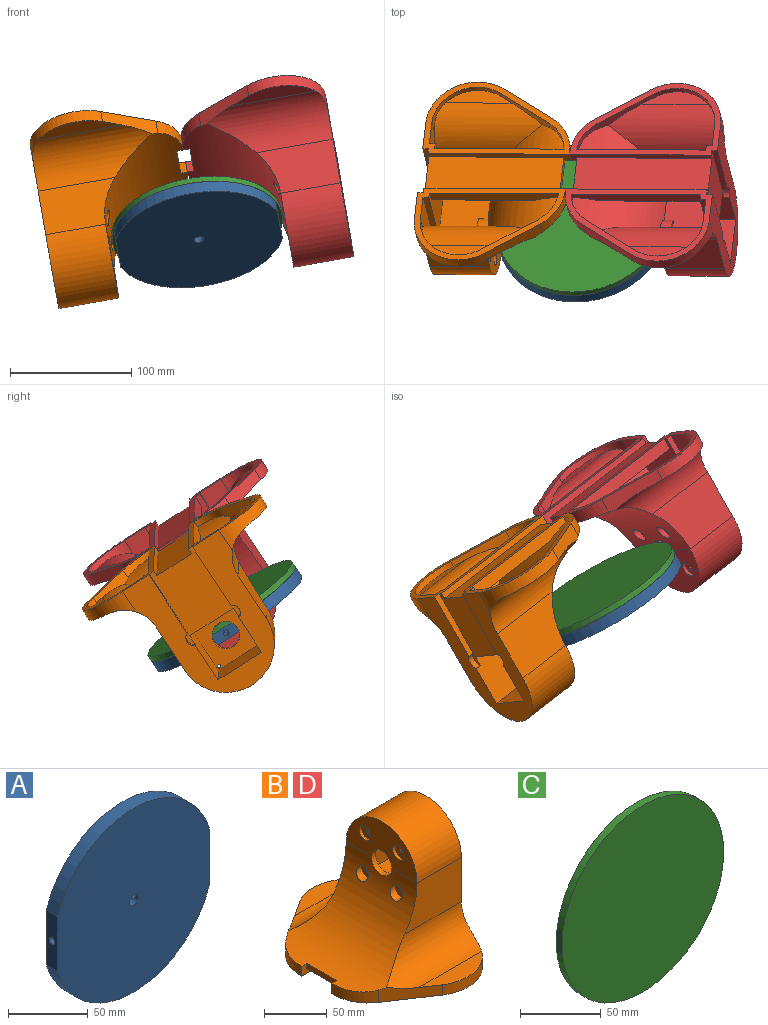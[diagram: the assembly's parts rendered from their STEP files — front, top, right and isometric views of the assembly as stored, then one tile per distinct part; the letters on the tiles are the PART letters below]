
ASSEMBLY  parts=4 mates=3
PART A: 14 faces, bbox 135x10.1x141.4 mm
  f0: cylinder r=2.5mm len=64.4mm, axis (-1,0,0), area 927.1mm2, adj f3,f9,f10,f11,f12,f13
  f1: cylinder r=2.5mm len=64.4mm, axis (-1,0,0), area 927.1mm2, adj f5,f9,f10,f11,f12,f13
  f2: plane 96.2x96.2mm, normal (0,1,0), area 7217.6mm2, adj f9,f11
  f3: plane 42x10mm, normal (1,0,0), area 400.4mm2, adj f0,f4,f6,f7,f8
  f4: cylinder r=70.71mm len=135.04mm, axis (0,1,0), area 1795mm2, adj f3,f5,f7,f8
  f5: plane 42x10mm, normal (-1,0,0), area 400.4mm2, adj f1,f4,f6,f7,f8
  f6: cylinder r=70.71mm len=135.04mm, axis (0,1,0), area 1795mm2, adj f3,f5,f7,f8
  f7: plane 141.42x135.04mm, normal (0,-1,0), area 15478.2mm2, adj f3,f4,f5,f6,f9
  f8: plane 141.42x135.04mm, normal (0,1,0), area 5641.8mm2, adj f3,f4,f5,f6,f12
  f9: cylinder r=4mm len=10mm, axis (0,1,0), area 209.8mm2, adj f0,f1,f2,f7
  f10: torus R=52.1mm, axis (0,-1,0), area 2003mm2, adj f0,f1,f11,f12
  f11: cylinder r=48.1mm len=96.2mm, axis (0,-1,0), area 816.8mm2, adj f0,f1,f2,f10,f13
  f12: cylinder r=56.1mm len=112.2mm, axis (0,-1,0), area 952.8mm2, adj f0,f1,f8,f10,f13
  f13: torus R=52.1mm, axis (0,-1,0), area 2003mm2, adj f0,f1,f11,f12
PART B: 93 faces, bbox 123.2x174.5x123.4 mm
  f0: plane 10x1.55mm, normal (-1,0,0), area 15.5mm2, adj f1,f2,f9,f36
  f1: cylinder r=73.21mm len=110.84mm, axis (0,1,0), area 9260.8mm2, adj f0,f7,f9,f11,f16,f17,f18,f21
  f2: plane 123.21x70.24mm, normal (0,0,-1), area 1573.2mm2, adj f0,f9,f10,f30,f35,f36,f43,f45
  f3: plane 123.21x70.24mm, normal (0,0,-1), area 1573.2mm2, adj f7,f10,f11,f32,f34,f38,f42,f45
  f4: plane 45.4x42.8mm, normal (0,-1,0), area 1901.8mm2, adj f6,f10,f19,f20,f44,f45
  f5: plane 45.4x42.8mm, normal (0,1,0), area 1901.8mm2, adj f6,f10,f19,f20,f41,f45
  f6: plane 42.8x40.5mm, normal (0,0,1), area 1733.4mm2, adj f4,f5,f20,f45
  f7: plane 118.31x10.21mm, normal (0,1,0), area 619.4mm2, adj f1,f3,f8,f11,f45,f84
  f8: plane 112.81x34mm, normal (0,0,-1), area 3835.6mm2, adj f7,f9,f45,f84
  f9: plane 118.31x10.21mm, normal (0,-1,0), area 619.4mm2, adj f0,f1,f2,f8,f45,f84
  f10: plane 123.36x94.48mm, normal (1,0,0), area 5011.8mm2, adj f2,f3,f4,f5,f17,f18,f19,f34
  f11: plane 10x1.55mm, normal (-1,0,0), area 15.5mm2, adj f1,f3,f7,f38
  f12: cylinder r=1.5mm len=3mm, axis (1,0,0), area 14.1mm2, adj f20,f25
  f13: cylinder r=1.5mm len=3mm, axis (1,0,0), area 14.1mm2, adj f20,f23
  f14: cylinder r=1.5mm len=3mm, axis (1,0,0), area 14.1mm2, adj f20,f29
  f15: cylinder r=1.5mm len=3mm, axis (1,0,0), area 14.1mm2, adj f20,f27
  f16: plane 80x40.15mm, normal (-1,0,0), area 2051.7mm2, adj f1,f17,f18,f21,f22,f24,f37
  f17: plane 64.11x43.36mm, normal (0,-1,0), area 2362.6mm2, adj f1,f10,f16,f37,f39
  f18: plane 64.11x43.36mm, normal (0,1,0), area 2362.6mm2, adj f1,f10,f16,f37,f40
  f19: plane 45.4x42.8mm, normal (0,0,-1), area 1943.1mm2, adj f4,f5,f10,f20
  f20: plane 42.8x42.8mm, normal (1,0,0), area 1388.1mm2, adj f4,f5,f6,f12,f13,f14,f15,f19
  f21: cylinder r=11.5mm len=23mm, axis (1,0,0), area 348.8mm2, adj f1,f16,f20
  f22: cylinder r=6.5mm len=13mm, axis (1,0,0), area 126.6mm2, adj f16,f23
  f23: plane 13x13mm, normal (-1,0,0), area 125.7mm2, adj f13,f22
  f24: cylinder r=6.5mm len=13mm, axis (1,0,0), area 126.6mm2, adj f16,f25
  f25: plane 13x13mm, normal (-1,0,0), area 125.7mm2, adj f12,f24
  f26: cylinder r=6.5mm len=13mm, axis (1,0,0), area 235.6mm2, adj f1,f27
  f27: plane 13x13mm, normal (-1,0,0), area 125.7mm2, adj f15,f26
  f28: cylinder r=6.5mm len=13mm, axis (1,0,0), area 235.6mm2, adj f1,f29
  f29: plane 13x13mm, normal (-1,0,0), area 125.7mm2, adj f14,f28
  f30: plane 43.23x28.71mm, normal (-0.55,0.83,0), area 570mm2, adj f1,f2,f31,f35,f36,f40
  f31: plane 70.92x17.24mm, normal (0,0,1), area 815.9mm2, adj f30,f35,f40
  f32: plane 43.23x28.71mm, normal (-0.55,-0.83,0), area 570mm2, adj f1,f3,f33,f34,f38,f39
  f33: plane 70.92x17.24mm, normal (0,0,1), area 815.9mm2, adj f32,f34,f39
  f34: cylinder r=40mm len=62.13mm, axis (0,0,-1), area 936.8mm2, adj f3,f10,f32,f33,f39
  f35: cylinder r=40mm len=62.13mm, axis (0,0,1), area 936.8mm2, adj f2,f10,f30,f31,f40
  f36: cylinder r=40mm len=33.32mm, axis (0,0,-1), area 412mm2, adj f0,f1,f2,f30
  f37: cylinder r=40mm len=80mm, axis (1,0,0), area 6283.2mm2, adj f10,f16,f17,f18
  f38: cylinder r=40mm len=33.32mm, axis (0,0,1), area 412mm2, adj f1,f3,f11,f32
  f39: cylinder r=30mm len=99.99mm, axis (-1,0,0), area 3860mm2, adj f1,f10,f17,f32,f33,f34
  f40: cylinder r=30mm len=99.99mm, axis (1,0,0), area 3860mm2, adj f1,f10,f18,f30,f31,f35
  f41: cylinder r=6.5mm len=12.06mm, axis (1,0,0), area 75.7mm2, adj f5,f10,f42,f45
  f42: plane 58.19x4.9mm, normal (0,1,0), area 285.1mm2, adj f3,f10,f41,f45
  f43: plane 58.19x4.9mm, normal (0,-1,0), area 285.1mm2, adj f2,f10,f44,f45
  f44: cylinder r=6.5mm len=12.06mm, axis (1,0,0), area 75.7mm2, adj f4,f10,f43,f45
  f45: plane 70.25x51mm, normal (1,0,0), area 2553.5mm2, adj f2,f3,f4,f5,f6,f7,f8,f9
  f46: plane 73.01x61mm, normal (-1,0,0), area 2665.9mm2, adj f2,f3,f47,f48,f49,f50,f70,f71
  f47: cylinder r=11.5mm len=17.56mm, axis (1,0,0), area 97.9mm2, adj f46,f48,f69,f81
  f48: plane 55.45x4.9mm, normal (0,1,0), area 271.7mm2, adj f2,f46,f47,f69
  f49: plane 55.45x4.9mm, normal (0,-1,0), area 271.7mm2, adj f3,f46,f50,f74
  f50: cylinder r=11.5mm len=17.56mm, axis (1,0,0), area 97.9mm2, adj f46,f49,f74,f78
  f51: cylinder r=35mm len=90.93mm, axis (1,0,0), area 3925mm2, adj f55,f59,f60,f66,f69,f82
  f52: cylinder r=35mm len=90.93mm, axis (-1,0,0), area 3925mm2, adj f56,f57,f58,f67,f74,f82
  f53: cylinder r=35mm len=25.7mm, axis (0,0,1), area 183.4mm2, adj f3,f58,f72,f82
  f54: cylinder r=35mm len=25.7mm, axis (0,0,-1), area 183.4mm2, adj f2,f60,f70,f82
  f55: cylinder r=35mm len=54.36mm, axis (0,0,1), area 439.2mm2, adj f2,f51,f59,f60,f69
  f56: cylinder r=35mm len=54.36mm, axis (0,0,-1), area 439.2mm2, adj f3,f52,f57,f58,f74
  f57: plane 55.58x12.24mm, normal (0,0,-1), area 457.2mm2, adj f52,f56,f58
  f58: plane 43.24x28.72mm, normal (0.55,0.83,0), area 340.9mm2, adj f3,f52,f53,f56,f57,f82
  f59: plane 55.58x12.24mm, normal (0,0,-1), area 457.2mm2, adj f51,f55,f60
  f60: plane 43.24x28.72mm, normal (0.55,-0.83,0), area 340.9mm2, adj f2,f51,f54,f55,f59,f82
  f61: cylinder r=11.5mm len=20.3mm, axis (1,0,0), area 272.4mm2, adj f73,f78,f82,f83
  f62: plane 20.3x20.3mm, normal (1,0,0), area 99.3mm2, adj f63,f73,f81
  f63: cylinder r=11.5mm len=20.3mm, axis (1,0,0), area 272.4mm2, adj f62,f73,f81,f82
  f64: plane 12.93x4mm, normal (1,0,0), area 31mm2, adj f65,f77,f78
  f65: cylinder r=11.5mm len=7.29mm, axis (1,0,0), area 26.4mm2, adj f64,f75,f77,f78
  f66: plane 53.02x43.36mm, normal (0,-1,0), area 1915.1mm2, adj f51,f68,f69,f76,f82
  f67: plane 53.02x43.36mm, normal (0,1,0), area 1915.1mm2, adj f52,f74,f75,f77,f82
  f68: plane 17.49x8.6mm, normal (1,0,0), area 105.6mm2, adj f66,f76,f79,f81,f82
  f69: plane 106.34x20.84mm, normal (-1,0,0), area 1062.8mm2, adj f2,f47,f48,f51,f55,f66,f76,f81
  f70: plane 108.14x10mm, normal (0,1,0), area 1014.6mm2, adj f2,f46,f54,f71,f82
  f71: plane 85.8x44mm, normal (0,0,1), area 3775mm2, adj f46,f70,f72,f82
  f72: plane 108.14x10mm, normal (0,-1,0), area 1014.6mm2, adj f3,f46,f53,f71,f82
  f73: plane 52.8x39.69mm, normal (0,0,-1), area 1846.4mm2, adj f46,f61,f62,f63,f78,f81,f82,f83
  f74: plane 106.34x20.84mm, normal (-1,0,0), area 1062.8mm2, adj f3,f49,f50,f52,f56,f67,f77,f78
  f75: plane 17.49x8.6mm, normal (1,0,0), area 105.6mm2, adj f65,f67,f77,f78,f82
  f76: cylinder r=35mm len=40mm, axis (1,0,0), area 981.3mm2, adj f66,f68,f69,f79,f80,f81
  f77: cylinder r=35mm len=40mm, axis (1,0,0), area 981.3mm2, adj f64,f65,f67,f74,f75,f78
  f78: plane 49.53x40.67mm, normal (0,-1,0), area 1813.6mm2, adj f46,f50,f61,f64,f65,f73,f74,f75
  f79: cylinder r=11.5mm len=7.29mm, axis (1,0,0), area 26.4mm2, adj f68,f76,f80,f81
  f80: plane 12.93x4mm, normal (1,0,0), area 31mm2, adj f76,f79,f81
  f81: plane 49.53x40.67mm, normal (0,1,0), area 1813.6mm2, adj f46,f47,f62,f63,f68,f69,f73,f76
  f82: cylinder r=78.21mm len=104.23mm, axis (0,1,0), area 6550.2mm2, adj f51,f52,f53,f54,f58,f60,f61,f63
  f83: plane 20.3x20.3mm, normal (1,0,0), area 99.3mm2, adj f61,f73,f78
  f84: plane 34x5.21mm, normal (-1,0,0), area 177mm2, adj f1,f7,f8,f9
  f85: plane 46.29x40mm, normal (0,0,1), area 1771.4mm2, adj f86,f87,f88,f89,f90,f91,f92
  f86: plane 12.95x4.01mm, normal (1,0,0), area 31.2mm2, adj f85,f87,f89
  f87: cylinder r=11.5mm len=7.38mm, axis (1,0,0), area 26.7mm2, adj f85,f86,f89,f90
  f88: cylinder r=11.5mm len=7.38mm, axis (1,0,0), area 26.7mm2, adj f85,f89,f90,f92
  f89: cylinder r=35mm len=46.29mm, axis (1,0,0), area 1980.6mm2, adj f85,f86,f87,f88,f90,f91,f92
  f90: plane 35.16x8.75mm, normal (1,0,0), area 215mm2, adj f85,f87,f88,f89
  f91: plane 46.29x8.75mm, normal (-1,0,0), area 277.5mm2, adj f85,f89
  f92: plane 12.95x4.01mm, normal (1,0,0), area 31.2mm2, adj f85,f88,f89
PART C: 3 faces, bbox 141.4x5x141.4 mm
  f0: cylinder r=70.71mm len=141.42mm, axis (0,-1,0), area 2221.4mm2, adj f1,f2
  f1: plane 141.42x141.42mm, normal (0,1,0), area 15708mm2, adj f0
  f2: plane 141.42x141.42mm, normal (0,-1,0), area 15708mm2, adj f0
PART D: same geometry as B
PLACE A rot(axis=(-0.04,0.88,0.48),171deg) t=(-396.1,-196.15,96.83)mm
PLACE B rot(axis=(0.03,0.96,-0.28),170.5deg) t=(-391.67,-165.28,71.29)mm
PLACE C rot(axis=(-1,-0.04,-0.09),123.1deg) t=(-396.82,-193.44,100.97)mm
PLACE D rot(axis=(1,-0.03,0.09),147.3deg) t=(-399.64,-232.45,114)mm
MATE revolute C.f0 <-> A.f9  axis (0.14,-0.54,-0.83) through (-396.1,-196.15,96.83)mm
MATE fastened D.f3 <-> B.f2  axis (0.14,-0.54,-0.83) through (-405.8,-139.4,152.43)mm
MATE revolute B.f21 <-> A.f0  axis (-0.98,0.01,-0.17) through (-466.81,-198.4,80.11)mm
